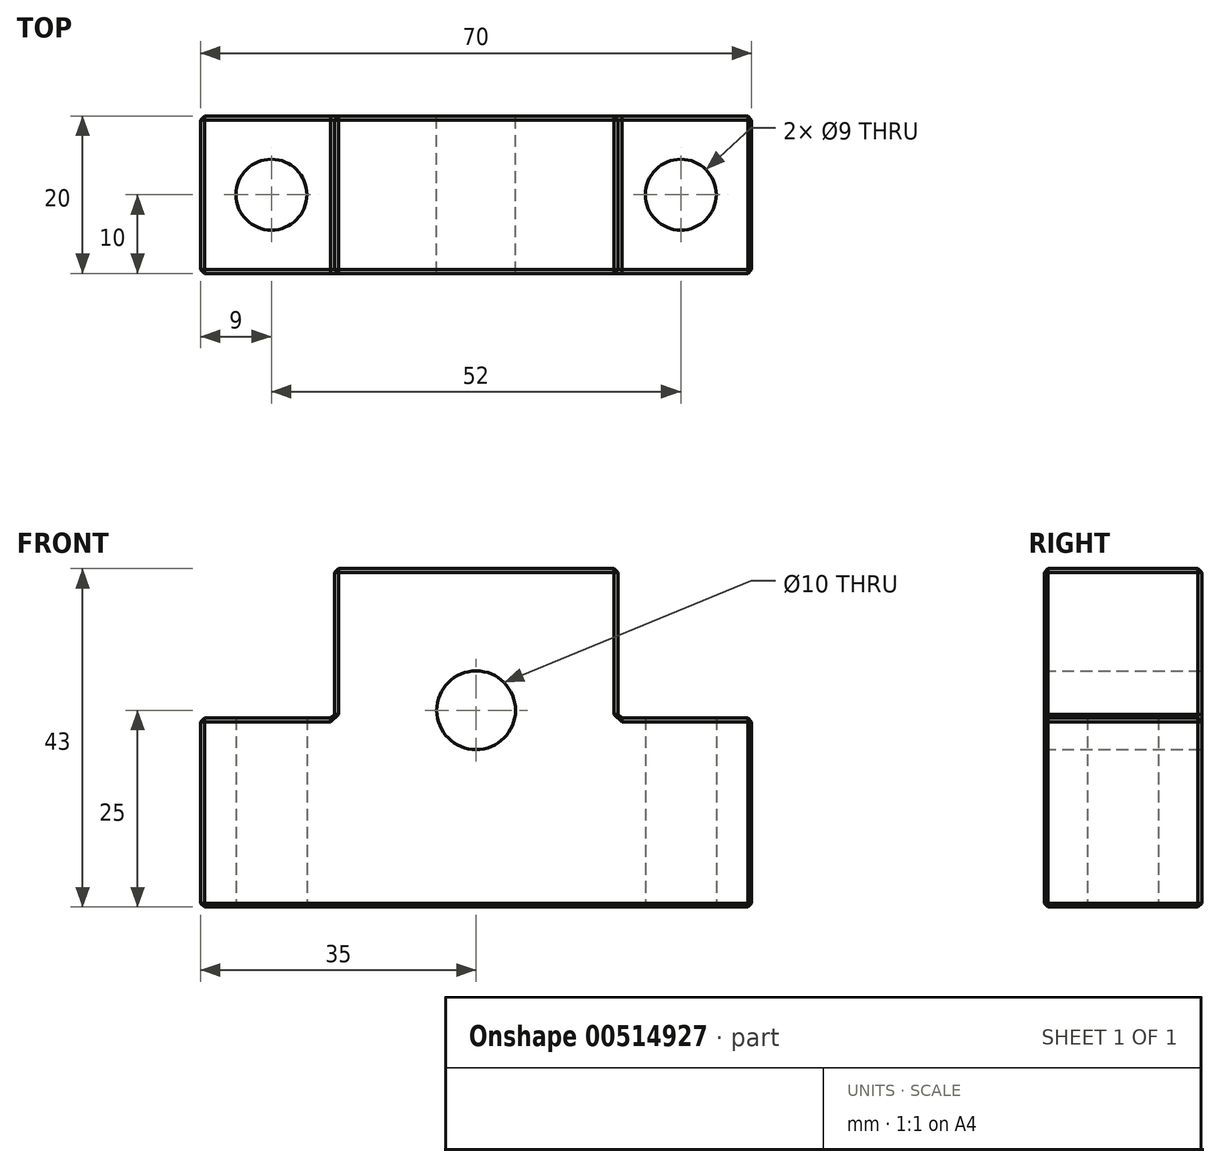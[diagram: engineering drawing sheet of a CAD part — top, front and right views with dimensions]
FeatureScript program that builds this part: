
annotation { "Feature Type Name" : "Feature", "Feature Type Description" : "" }
export const myFeature = defineFeature(function(context is Context, id is Id, definition is map)
    precondition{}
    {
        {
            var Q0;
            Q0=qCreatedBy(makeId("Front.planeOp"),FACE);
            var sketch = newSketch(context, id + "F0", { "sketchPlane" : qUnion([Q0])});
            skCircle(sketch, "E0", {"center": v(0, 0) * mm, "radius": 5 * mm});
            skLineSegment(sketch, "E1", {"start": v(0, 33.47) * mm, "end": v(0, -35.9) * mm, "construction": true});
            skLineSegment(sketch, "E2", {"start": v(0, 18) * mm, "end": v(18, 18) * mm});
            skLineSegment(sketch, "E3", {"start": v(18, 18) * mm, "end": v(18, -1) * mm});
            skLineSegment(sketch, "E4", {"start": v(18, -1) * mm, "end": v(35, -1) * mm});
            skLineSegment(sketch, "E5", {"start": v(35, -1) * mm, "end": v(35, -25) * mm});
            skLineSegment(sketch, "E6", {"start": v(35, -25) * mm, "end": v(0, -25) * mm});
            skLineSegment(sketch, "E7.MirrorCS", {"start": v(0, 18) * mm, "end": v(-18, 18) * mm});
            skLineSegment(sketch, "E8.MirrorCS", {"start": v(-18, 18) * mm, "end": v(-18, -1) * mm});
            skLineSegment(sketch, "E9.MirrorCS", {"start": v(-18, -1) * mm, "end": v(-35, -1) * mm});
            skLineSegment(sketch, "E10.MirrorCS", {"start": v(-35, -1) * mm, "end": v(-35, -25) * mm});
            skLineSegment(sketch, "E11.MirrorCS", {"start": v(-35, -25) * mm, "end": v(0, -25) * mm});
            skSolve(sketch);
        }
        {
            var Q0;
            Q0=makeQuery(id+"F0.imprint","IMPRINT",FACE,{"disambiguationData":[TD([[makeQuery(id+"F0.imprint","IMPRINT",EDGE,{"derivedFrom":sQuery(id+"F0.wireOp",EDGE,"E0")}),-1.0]])]});
            extrude(context, id + "F1", {"entities" : qUnion([Q0]), "endBound" : BoundingType.SYMMETRIC, "depth" : 20 * mm, "offsetDistance" : 25 * mm});
        }
        {
            var Q0;
            Q0=makeQuery(id+"F1.opExtrude","SWEPT_FACE",FACE,{"disambiguationData":[OSD([sQuery(id+"F0.wireOp",EDGE,"E2"),sQuery(id+"F0.wireOp",EDGE,"E7.MirrorCS")])]});
            var Q1;
            Q1=makeQuery(id+"F1.opExtrude","SWEPT_FACE",FACE,{"disambiguationData":[OSD([sQuery(id+"F0.wireOp",EDGE,"E9.MirrorCS")])]});
            var Q2;
            Q2=makeQuery(id+"F1.opExtrude","SWEPT_FACE",FACE,{"disambiguationData":[OSD([sQuery(id+"F0.wireOp",EDGE,"E8.MirrorCS")])]});
            var Q3;
            Q3=makeQuery(id+"F1.opExtrude","SWEPT_FACE",FACE,{"disambiguationData":[OSD([sQuery(id+"F0.wireOp",EDGE,"E10.MirrorCS")])]});
            var Q4;
            Q4=makeQuery(id+"F1.opExtrude","SWEPT_FACE",FACE,{"disambiguationData":[OSD([sQuery(id+"F0.wireOp",EDGE,"E5")])]});
            var Q5;
            Q5=makeQuery(id+"F1.opExtrude","SWEPT_FACE",FACE,{"disambiguationData":[OSD([sQuery(id+"F0.wireOp",EDGE,"E3")])]});
            var Q6;
            Q6=makeQuery(id+"F1.opExtrude","SWEPT_FACE",FACE,{"disambiguationData":[OSD([sQuery(id+"F0.wireOp",EDGE,"E4")])]});
            var Q7;
            Q7=makeQuery(id+"F1.opExtrude","SWEPT_FACE",FACE,{"disambiguationData":[OSD([sQuery(id+"F0.wireOp",EDGE,"E6"),sQuery(id+"F0.wireOp",EDGE,"E11.MirrorCS")])]});
            chamfer(context, id + "F2", {"entities" : qUnion([Q0, Q1, Q2, Q3, Q4, Q5, Q6, Q7]), "width" : 0.5 * mm, "tangentPropagation" : true});
        }
        {
            var Q0;
            Q0=makeQuery(id+"F1.opExtrude","SWEPT_FACE",FACE,{"disambiguationData":[OSD([sQuery(id+"F0.wireOp",EDGE,"E6"),sQuery(id+"F0.wireOp",EDGE,"E11.MirrorCS")])]});
            var sketch = newSketch(context, id + "F3", { "sketchPlane" : qUnion([Q0])});
            skPoint(sketch, "E12", {"position": v(-26, 0) * mm});
            skPoint(sketch, "E13", {"position": v(26, 0) * mm});
            skSolve(sketch);
        }
        {
            var Q0;
            Q0=sQuery(id+"F3.wireOp",VERTEX,"E12");
            var Q1;
            Q1=sQuery(id+"F3.wireOp",VERTEX,"E13");
            var Q2;
            Q2=makeQuery(id+"F1.opExtrude","SWEPT_BODY",BODY,{"disambiguationData":[OSD([sQuery(id+"F0.wireOp",EDGE,"E0"),sQuery(id+"F0.wireOp",EDGE,"E2"),sQuery(id+"F0.wireOp",EDGE,"E3"),sQuery(id+"F0.wireOp",EDGE,"E4"),sQuery(id+"F0.wireOp",EDGE,"E5"),sQuery(id+"F0.wireOp",EDGE,"E6"),sQuery(id+"F0.wireOp",EDGE,"E7.MirrorCS"),sQuery(id+"F0.wireOp",EDGE,"E8.MirrorCS"),sQuery(id+"F0.wireOp",EDGE,"E9.MirrorCS"),sQuery(id+"F0.wireOp",EDGE,"E10.MirrorCS"),sQuery(id+"F0.wireOp",EDGE,"E11.MirrorCS")])]});
            hole(context, id + "F4", {"style" : HoleStyle.SIMPLE, "endStyle" : HoleEndStyle.THROUGH, "holeDiameter" : 9 * mm, "majorDiameter" : 5 * mm, "isTappedThrough" : true, "tappedDepth" : 12 * mm, "tapClearance" : 3, "locations" : qUnion([Q0, Q1]), "scope" : qUnion([Q2])});
        }
    });
